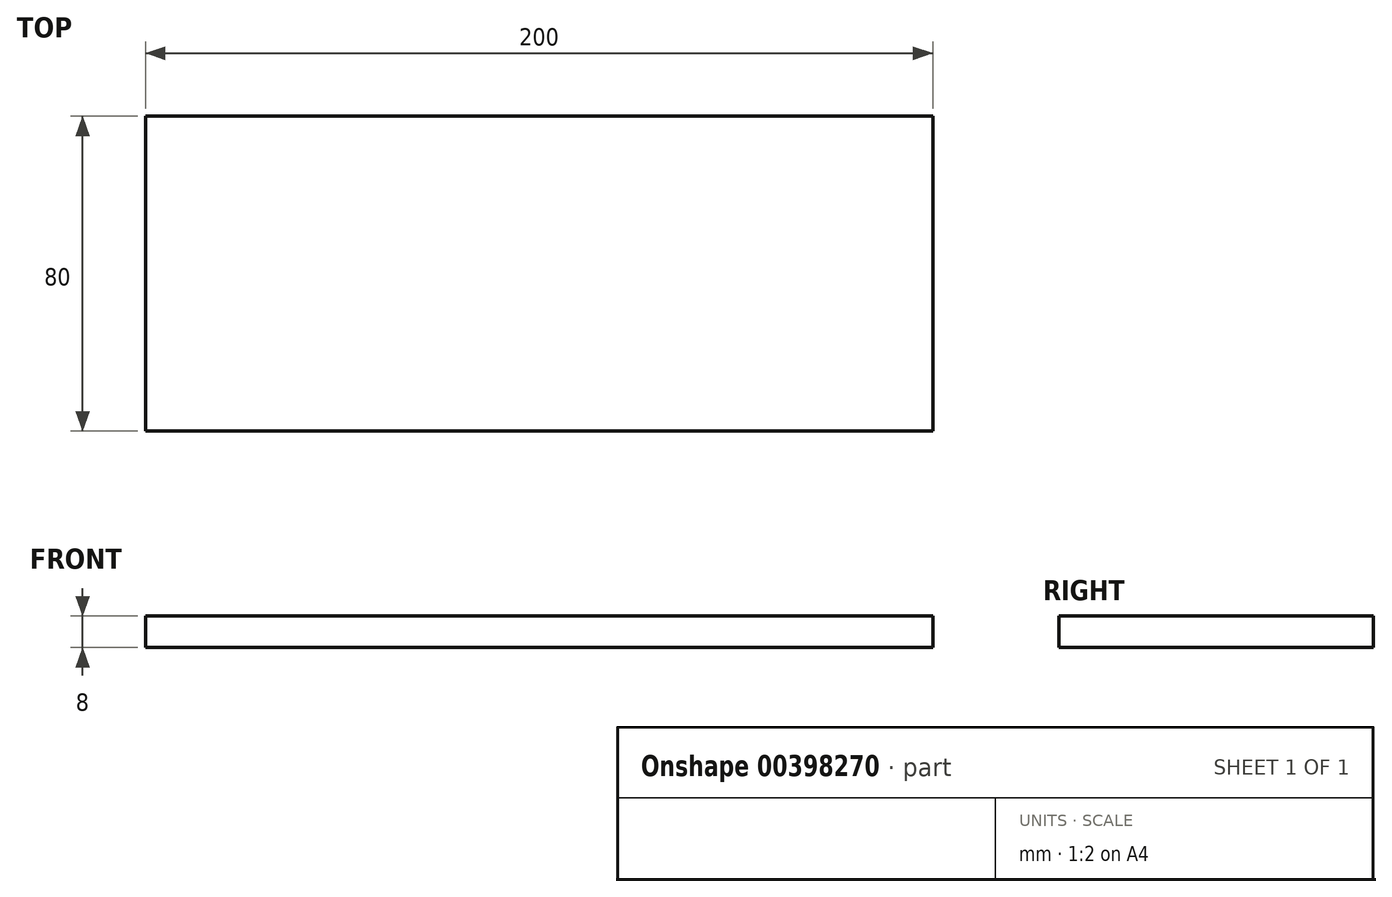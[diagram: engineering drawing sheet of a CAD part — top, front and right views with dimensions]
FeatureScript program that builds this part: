
annotation { "Feature Type Name" : "Feature", "Feature Type Description" : "" }
export const myFeature = defineFeature(function(context is Context, id is Id, definition is map)
    precondition{}
    {
        {
            var Q0;
            Q0=qCreatedBy(makeId("Top.planeOp"),FACE);
            var sketch = newSketch(context, id + "F0", { "sketchPlane" : qUnion([Q0])});
            skLineSegment(sketch, "E0.bottom", {"start": v(0, 0) * mm, "end": v(200, 0) * mm});
            skLineSegment(sketch, "E0.top", {"start": v(0, 80) * mm, "end": v(200, 80) * mm});
            skLineSegment(sketch, "E0.left", {"start": v(0, 0) * mm, "end": v(0, 80) * mm});
            skLineSegment(sketch, "E0.right", {"start": v(200, 0) * mm, "end": v(200, 80) * mm});
            skSolve(sketch);
        }
        {
            var Q0;
            Q0 = qSketchRegion(id + "F0", true);
            extrude(context, id + "F1", {"entities" : qUnion([Q0]), "depth" : 8 * mm});
        }
    });
